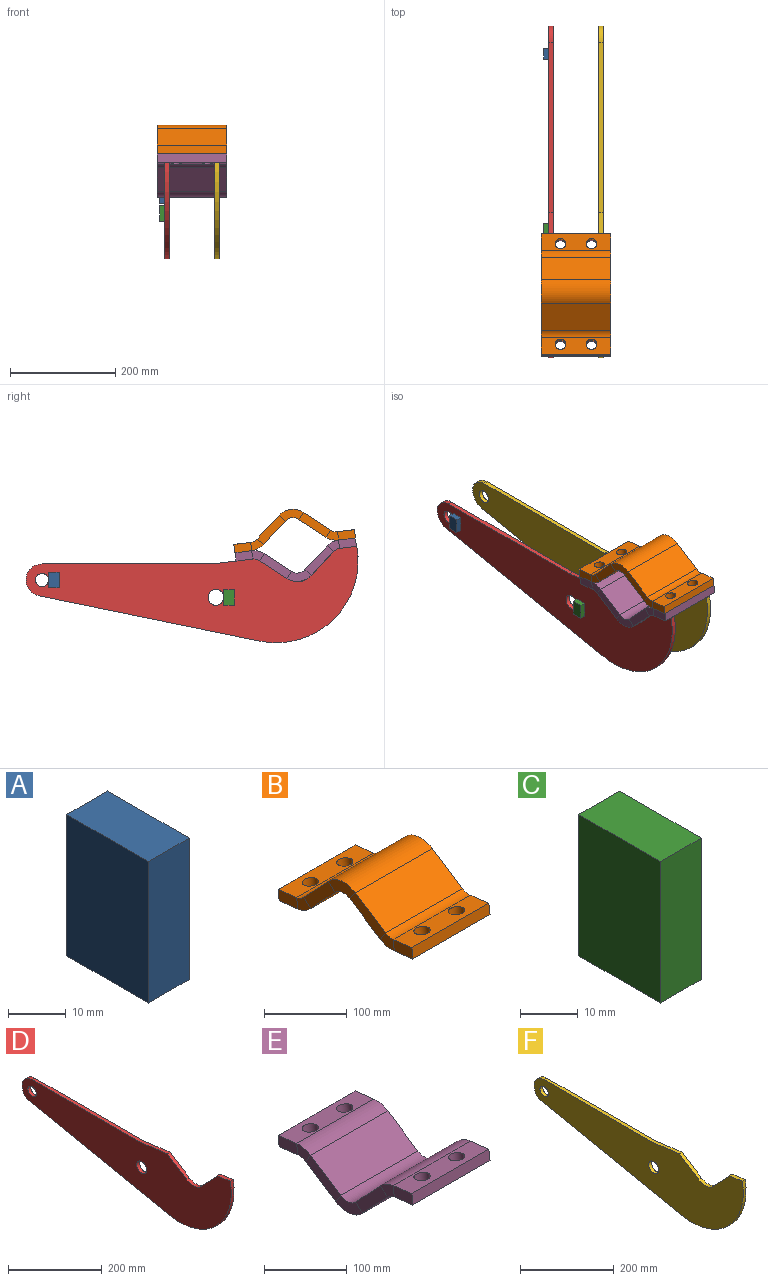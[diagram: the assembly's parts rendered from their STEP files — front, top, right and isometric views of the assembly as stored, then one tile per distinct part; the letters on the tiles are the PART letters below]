
ASSEMBLY  parts=6 mates=5
PART A: 6 faces, bbox 10x20x30 mm
  f0: plane 20x10mm, normal (0,0,1), area 200mm2, adj f1,f3,f4,f5
  f1: plane 30x10mm, normal (0,1,0), area 300mm2, adj f0,f2,f4,f5
  f2: plane 20x10mm, normal (0,0,-1), area 200mm2, adj f1,f3,f4,f5
  f3: plane 30x10mm, normal (0,-1,0), area 300mm2, adj f0,f2,f4,f5
  f4: plane 30x20mm, normal (-1,0,0), area 600mm2, adj f0,f1,f2,f3
  f5: plane 30x20mm, normal (1,0,0), area 600mm2, adj f0,f1,f2,f3
PART B: 34 faces, bbox 132x231.2x82.8 mm
  f0: plane 33.91x19.81mm, normal (1,0,0), area 515.2mm2, adj f1,f5,f6,f31
  f1: plane 132x15.88mm, normal (0,0.99,-0.12), area 2112mm2, adj f0,f2,f5,f6
  f2: plane 33.91x19.81mm, normal (-1,0,0), area 515.2mm2, adj f1,f5,f6,f30
  f3: cylinder r=10mm len=21.8mm, axis (0,0.12,0.99), area 1005.3mm2, adj f5,f6
  f4: cylinder r=10mm len=21.8mm, axis (0,0.12,0.99), area 1005.3mm2, adj f5,f6
  f5: plane 132x31.96mm, normal (0,0.12,0.99), area 3622.2mm2, adj f0,f1,f2,f3,f4,f33
  f6: plane 132x31.96mm, normal (0,-0.12,-0.99), area 3622.2mm2, adj f0,f1,f2,f3,f4,f32
  f7: plane 56.12x53.75mm, normal (1,0,0), area 987.9mm2, adj f9,f10,f27,f31
  f8: plane 56.12x53.75mm, normal (-1,0,0), area 987.9mm2, adj f9,f10,f26,f30
  f9: plane 132x45.23mm, normal (0,0.73,0.68), area 8150mm2, adj f7,f8,f28,f33
  f10: plane 132x45.23mm, normal (0,-0.73,-0.68), area 8150mm2, adj f7,f8,f29,f32
  f11: plane 60.46x47.12mm, normal (1,0,0), area 987.9mm2, adj f13,f14,f23,f27
  f12: plane 60.46x47.12mm, normal (-1,0,0), area 987.9mm2, adj f13,f14,f22,f26
  f13: plane 132x51.72mm, normal (0,-0.55,0.84), area 8150mm2, adj f11,f12,f25,f28
  f14: plane 132x51.72mm, normal (0,0.55,-0.84), area 8150mm2, adj f11,f12,f24,f29
  f15: plane 33.91x19.81mm, normal (1,0,0), area 515.2mm2, adj f19,f20,f21,f23
  f16: plane 33.91x19.81mm, normal (-1,0,0), area 515.2mm2, adj f19,f20,f21,f22
  f17: cylinder r=10mm len=21.8mm, axis (0,0.12,0.99), area 1005.3mm2, adj f20,f21
  f18: cylinder r=10mm len=21.8mm, axis (0,0.12,0.99), area 1005.3mm2, adj f20,f21
  f19: plane 132x15.88mm, normal (0,-0.99,0.12), area 2112mm2, adj f15,f16,f20,f21
  f20: plane 132x31.96mm, normal (0,0.12,0.99), area 3622.2mm2, adj f15,f16,f17,f18,f19,f25
  f21: plane 132x31.96mm, normal (0,-0.12,-0.99), area 3622.2mm2, adj f15,f16,f17,f18,f19,f24
  f22: plane 24.05x19.25mm, normal (-1,0,0), area 313.6mm2, adj f12,f16,f24,f25
  f23: plane 24.05x19.25mm, normal (1,0,0), area 313.6mm2, adj f11,f15,f24,f25
  f24: cylinder r=36mm len=132mm, axis (-1,0,0), area 3325.9mm2, adj f14,f21,f22,f23
  f25: cylinder r=20mm len=132mm, axis (-1,0,0), area 1847.7mm2, adj f13,f20,f22,f23
  f26: plane 46.03x22.39mm, normal (-1,0,0), area 627.1mm2, adj f8,f12,f28,f29
  f27: plane 46.03x22.39mm, normal (1,0,0), area 627.1mm2, adj f7,f11,f28,f29
  f28: cylinder r=36mm len=132mm, axis (-1,0,0), area 6651.8mm2, adj f9,f13,f26,f27
  f29: cylinder r=20mm len=132mm, axis (-1,0,0), area 3695.4mm2, adj f10,f14,f26,f27
  f30: plane 23.93x22.12mm, normal (-1,0,0), area 313.6mm2, adj f2,f8,f32,f33
  f31: plane 23.93x22.12mm, normal (1,0,0), area 313.6mm2, adj f0,f7,f32,f33
  f32: cylinder r=36mm len=132mm, axis (-1,0,0), area 3325.9mm2, adj f6,f10,f30,f31
  f33: cylinder r=20mm len=132mm, axis (-1,0,0), area 1847.7mm2, adj f5,f9,f30,f31
PART C: 6 faces, bbox 10x20x30 mm
  f0: plane 30x10mm, normal (0,1,0), area 300mm2, adj f1,f3,f4,f5
  f1: plane 20x10mm, normal (0,0,-1), area 200mm2, adj f0,f2,f4,f5
  f2: plane 30x10mm, normal (0,-1,0), area 300mm2, adj f1,f3,f4,f5
  f3: plane 20x10mm, normal (0,0,1), area 200mm2, adj f0,f2,f4,f5
  f4: plane 30x20mm, normal (-1,0,0), area 600mm2, adj f0,f1,f2,f3
  f5: plane 30x20mm, normal (1,0,0), area 600mm2, adj f0,f1,f2,f3
PART D: 13 faces, bbox 8.5x632x183.6 mm
  f0: cylinder r=35mm len=44.75mm, axis (1,0,0), area 416.4mm2, adj f1,f9,f11,f12
  f1: plane 51.19x47.57mm, normal (0,0.73,0.68), area 594mm2, adj f0,f2,f11,f12
  f2: plane 39.21x8.5mm, normal (0,0.12,0.99), area 335.8mm2, adj f1,f3,f11,f12
  f3: cylinder r=155.62mm len=186.94mm, axis (1,0,0), area 2585.1mm2, adj f2,f4,f11,f12
  f4: plane 420.68x86.42mm, normal (0,0.2,-0.98), area 3650.5mm2, adj f3,f5,f11,f12
  f5: cylinder r=30.5mm len=60.38mm, axis (1,0,0), area 761.9mm2, adj f4,f6,f11,f12
  f6: plane 325x8.5mm, normal (0,0,1), area 2762.5mm2, adj f5,f7,f11,f12
  f7: plane 83.87x10.3mm, normal (0,0.12,0.99), area 718.3mm2, adj f6,f9,f11,f12
  f8: cylinder r=12.5mm len=25mm, axis (1,0,0), area 667.6mm2, adj f11,f12
  f9: plane 58.54x38.17mm, normal (0,-0.55,0.84), area 594mm2, adj f0,f7,f11,f12
  f10: cylinder r=15mm len=30mm, axis (1,0,0), area 801.1mm2, adj f11,f12
  f11: plane 631.98x183.61mm, normal (-1,0,0), area 66252.2mm2, adj f0,f1,f2,f3,f4,f5,f6,f7
  f12: plane 631.98x183.61mm, normal (1,0,0), area 66252.2mm2, adj f0,f1,f2,f3,f4,f5,f6,f7
PART E: 34 faces, bbox 132x231.2x82.8 mm
  f0: plane 33.91x19.81mm, normal (-1,0,0), area 515.2mm2, adj f1,f5,f6,f31
  f1: plane 132x15.88mm, normal (0,-0.99,0.12), area 2112mm2, adj f0,f2,f5,f6
  f2: plane 33.91x19.81mm, normal (1,0,0), area 515.2mm2, adj f1,f5,f6,f30
  f3: cylinder r=10mm len=21.8mm, axis (0,0.12,0.99), area 1005.3mm2, adj f5,f6
  f4: cylinder r=10mm len=21.8mm, axis (0,0.12,0.99), area 1005.3mm2, adj f5,f6
  f5: plane 132x31.96mm, normal (0,0.12,0.99), area 3622.2mm2, adj f0,f1,f2,f3,f4,f32
  f6: plane 132x31.96mm, normal (0,-0.12,-0.99), area 3622.2mm2, adj f0,f1,f2,f3,f4,f33
  f7: plane 56.12x53.75mm, normal (-1,0,0), area 987.9mm2, adj f9,f10,f27,f31
  f8: plane 56.12x53.75mm, normal (1,0,0), area 987.9mm2, adj f9,f10,f26,f30
  f9: plane 132x45.23mm, normal (0,0.73,0.68), area 8150mm2, adj f7,f8,f29,f32
  f10: plane 132x45.23mm, normal (0,-0.73,-0.68), area 8150mm2, adj f7,f8,f28,f33
  f11: plane 60.46x47.12mm, normal (-1,0,0), area 987.9mm2, adj f13,f14,f23,f27
  f12: plane 60.46x47.12mm, normal (1,0,0), area 987.9mm2, adj f13,f14,f22,f26
  f13: plane 132x51.72mm, normal (0,-0.55,0.84), area 8150mm2, adj f11,f12,f24,f29
  f14: plane 132x51.72mm, normal (0,0.55,-0.84), area 8150mm2, adj f11,f12,f25,f28
  f15: plane 33.91x19.81mm, normal (-1,0,0), area 515.2mm2, adj f19,f20,f21,f23
  f16: plane 33.91x19.81mm, normal (1,0,0), area 515.2mm2, adj f19,f20,f21,f22
  f17: cylinder r=10mm len=21.8mm, axis (0,0.12,0.99), area 1005.3mm2, adj f20,f21
  f18: cylinder r=10mm len=21.8mm, axis (0,0.12,0.99), area 1005.3mm2, adj f20,f21
  f19: plane 132x15.88mm, normal (0,0.99,-0.12), area 2112mm2, adj f15,f16,f20,f21
  f20: plane 132x31.96mm, normal (0,0.12,0.99), area 3622.2mm2, adj f15,f16,f17,f18,f19,f24
  f21: plane 132x31.96mm, normal (0,-0.12,-0.99), area 3622.2mm2, adj f15,f16,f17,f18,f19,f25
  f22: plane 24.05x19.25mm, normal (1,0,0), area 313.6mm2, adj f12,f16,f24,f25
  f23: plane 24.05x19.25mm, normal (-1,0,0), area 313.6mm2, adj f11,f15,f24,f25
  f24: cylinder r=36mm len=132mm, axis (1,0,0), area 3325.9mm2, adj f13,f20,f22,f23
  f25: cylinder r=20mm len=132mm, axis (1,0,0), area 1847.7mm2, adj f14,f21,f22,f23
  f26: plane 46.03x22.39mm, normal (1,0,0), area 627.1mm2, adj f8,f12,f28,f29
  f27: plane 46.03x22.39mm, normal (-1,0,0), area 627.1mm2, adj f7,f11,f28,f29
  f28: cylinder r=36mm len=132mm, axis (1,0,0), area 6651.8mm2, adj f10,f14,f26,f27
  f29: cylinder r=20mm len=132mm, axis (1,0,0), area 3695.4mm2, adj f9,f13,f26,f27
  f30: plane 23.93x22.12mm, normal (1,0,0), area 313.6mm2, adj f2,f8,f32,f33
  f31: plane 23.93x22.12mm, normal (-1,0,0), area 313.6mm2, adj f0,f7,f32,f33
  f32: cylinder r=36mm len=132mm, axis (1,0,0), area 3325.9mm2, adj f5,f9,f30,f31
  f33: cylinder r=20mm len=132mm, axis (1,0,0), area 1847.7mm2, adj f6,f10,f30,f31
PART F: 13 faces, bbox 8.5x632x183.6 mm
  f0: cylinder r=35mm len=44.75mm, axis (1,0,0), area 416.4mm2, adj f1,f9,f11,f12
  f1: plane 51.19x47.57mm, normal (0,0.73,0.68), area 594mm2, adj f0,f2,f11,f12
  f2: plane 39.21x8.5mm, normal (0,0.12,0.99), area 335.8mm2, adj f1,f3,f11,f12
  f3: cylinder r=155.62mm len=186.94mm, axis (1,0,0), area 2585.1mm2, adj f2,f4,f11,f12
  f4: plane 420.68x86.42mm, normal (0,0.2,-0.98), area 3650.5mm2, adj f3,f5,f11,f12
  f5: cylinder r=30.5mm len=60.38mm, axis (1,0,0), area 761.9mm2, adj f4,f6,f11,f12
  f6: plane 325x8.5mm, normal (0,0,1), area 2762.5mm2, adj f5,f7,f11,f12
  f7: plane 83.87x10.3mm, normal (0,0.12,0.99), area 718.3mm2, adj f6,f9,f11,f12
  f8: cylinder r=12.5mm len=25mm, axis (1,0,0), area 667.6mm2, adj f11,f12
  f9: plane 58.54x38.17mm, normal (0,-0.55,0.84), area 594mm2, adj f0,f7,f11,f12
  f10: cylinder r=15mm len=30mm, axis (1,0,0), area 801.1mm2, adj f11,f12
  f11: plane 631.98x183.61mm, normal (-1,0,0), area 66252.2mm2, adj f0,f1,f2,f3,f4,f5,f6,f7
  f12: plane 631.98x183.61mm, normal (1,0,0), area 66252.2mm2, adj f0,f1,f2,f3,f4,f5,f6,f7
PLACE A t=(0.55,-0.74,0.09)mm
PLACE B t=(0,-3.9,-31.76)mm
PLACE C t=(0.55,-0.74,1.5)mm
PLACE D t=(0.55,-0.74,0.09)mm
PLACE E at identity
PLACE F t=(0.75,-0.74,0.09)mm
MATE fastened A.f5 <-> D.f11  axis (1,0,0) through (-102.75,-23.24,0.09)mm
MATE fastened F.f2 <-> E.f6  axis (0,0.12,0.99) through (-3.5,-580.08,61.82)mm
MATE fastened D.f2 <-> E.f6  axis (0,0.12,0.99) through (-98.5,-580.08,61.82)mm
MATE fastened C.f5 <-> D.f11  axis (1,0,0) through (-102.75,-356.58,-33.11)mm
MATE fastened B.f17 <-> E.f4  axis (0,-0.12,-0.99) through (-21.5,-578.13,77.7)mm
